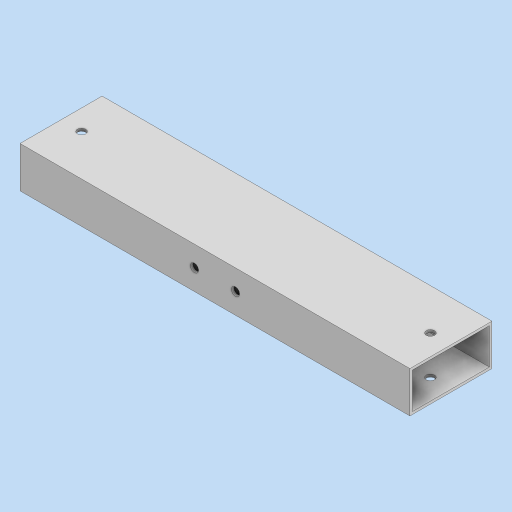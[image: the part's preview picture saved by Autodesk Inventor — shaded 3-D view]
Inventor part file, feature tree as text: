
AUTODESK INVENTOR PART (.ipt)
format: ipt  version: 2024 (Build 280153000, 153)  size: 126,464 bytes
history: native  units: in
note: dims shown in document units (in); Inventor stores cm internally (conversion verified against a paired STEP export)
features: extrude x3, sketch x3, projected_geometry x2
ambient origin geometry x8: Origin, YZ Plane, XZ Plane, XY Plane, X Axis, Y Axis, Z Axis, Center Point
bodies: Solid1 (feature_tree)
feature tree (8):
  extrude  "Extrusion1"  Depth=2.0in
  extrude  "Extrusion2"  Depth=9.5in TaperAngle=0.0deg
  extrude  "Extrusion4"  Depth=1.0in
  sketch  "Sketch1"  dims[d0=1.0in d1=2.0in]
  sketch  "Sketch2"  dims[d2=0.0625in d3=9.5in d4=0.0in]
  projected_geometry  "Projected Loop1"
  sketch  "Sketch4"  dims[d5=0.203in d6=0.5in d7=0.203in d8=0.5in d9=1.0in d10=1.0in d11=1.0in d12=0.0in d21=0.203in d22=0.203in d23=0.5in d24=1.0in d25=0.0in d26=0.0in d27=0.5in d28=0.5in]
  projected_geometry  "Projected Loop3"
